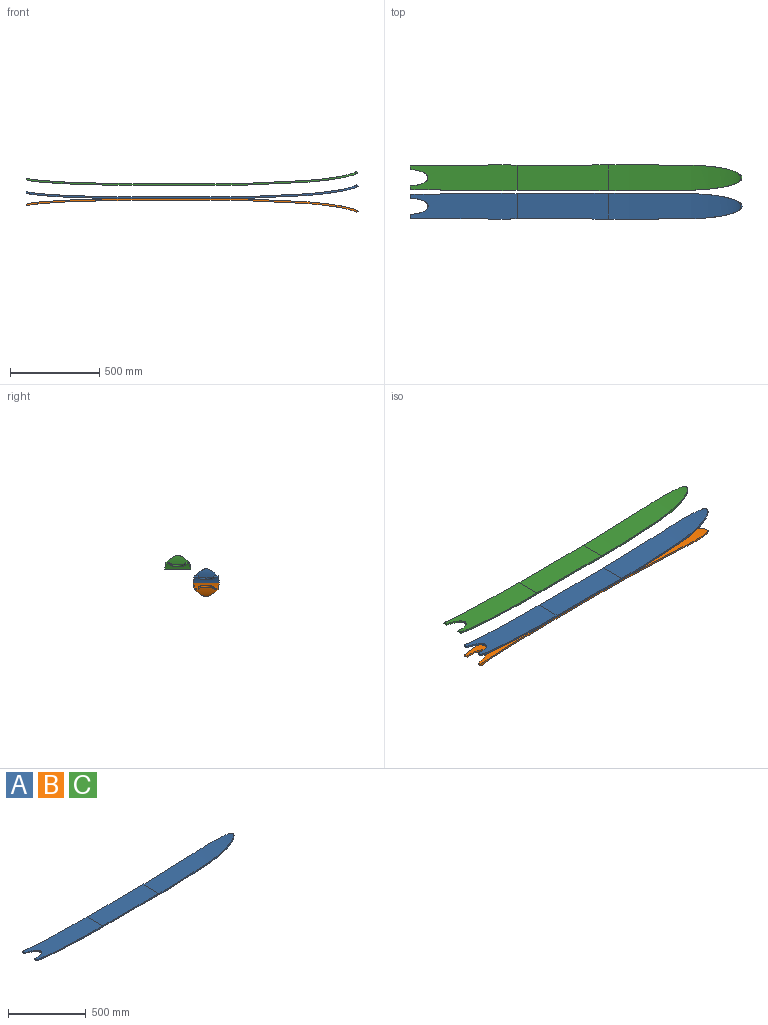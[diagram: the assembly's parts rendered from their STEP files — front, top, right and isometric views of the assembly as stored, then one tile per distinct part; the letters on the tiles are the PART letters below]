
ASSEMBLY  parts=3 mates=1
PART A: 24 faces, bbox 1860.1x145.9x78.2 mm
  f0: plane 21.12x9.66mm, normal (-0.97,0,0.26), area 211.2mm2, adj f1,f17,f18,f21
  f1: bspline ~100.87x90mm, area 2363.6mm2, adj f0,f2,f18,f21
  f2: plane 21.12x9.66mm, normal (-0.97,0,0.26), area 211.2mm2, adj f1,f3,f18,f21
  f3: bspline ~450.54x38.5mm, area 4506.2mm2, adj f2,f4,f18,f21
  f4: bspline ~106.3x11.07mm, area 1062.1mm2, adj f3,f5,f18,f21
  f5: bspline ~43.36x10.1mm, area 433.4mm2, adj f4,f6,f18,f21
  f6: cylinder r=25000mm len=510mm, axis (0,0,1), area 5100.1mm2, adj f5,f7,f19,f22
  f7: bspline ~10.01x9.26mm, area 92.6mm2, adj f6,f8,f20,f23
  f8: bspline ~105.57x10.94mm, area 1054.9mm2, adj f7,f9,f20,f23
  f9: bspline ~349.38x26.27mm, area 3493.7mm2, adj f8,f10,f20,f23
  f10: bspline ~286.82x140.12mm, area 6174.8mm2, adj f9,f11,f20,f23
  f11: bspline ~349.38x26.27mm, area 3493.7mm2, adj f10,f12,f20,f23
  f12: bspline ~105.57x10.94mm, area 1054.9mm2, adj f11,f13,f20,f23
  f13: bspline ~10.01x9.26mm, area 92.6mm2, adj f12,f14,f20,f23
  f14: cylinder r=25000mm len=510mm, axis (0,0,1), area 5100.1mm2, adj f13,f15,f19,f22
  f15: bspline ~43.36x10.1mm, area 433.4mm2, adj f14,f16,f18,f21
  f16: bspline ~106.3x11.07mm, area 1062.1mm2, adj f15,f17,f18,f21
  f17: bspline ~450.54x38.5mm, area 4512.6mm2, adj f0,f16,f18,f21
  f18: extruded ~597.41x143.23mm, area 76557.4mm2, adj f0,f1,f2,f3,f4,f5,f15,f16
  f19: plane 510x144.51mm, normal (0,0,1), area 72245mm2, adj f6,f14,f18,f20
  f20: extruded ~744.33x145.59mm, area 96890.1mm2, adj f7,f8,f9,f10,f11,f12,f13,f19
  f21: extruded ~600x143.23mm, area 76761.2mm2, adj f0,f1,f2,f3,f4,f5,f15,f16
  f22: plane 510x144.51mm, normal (0,0,-1), area 72245mm2, adj f6,f14,f21,f23
  f23: extruded ~750.06x145.59mm, area 98381.7mm2, adj f7,f8,f9,f10,f11,f12,f13,f22
PART B: same geometry as A
PART C: same geometry as A
PLACE A t=(-195.65,-385.39,163.73)mm
PLACE B rot(axis=(1,0,0),180deg) t=(-195.65,-385.39,-16.27)mm
PLACE C t=(-196.02,-225.86,238.45)mm
MATE fastened B.f22 <-> A.f22  axis (0,0,1) through (-269.98,-385.39,73.73)mm
